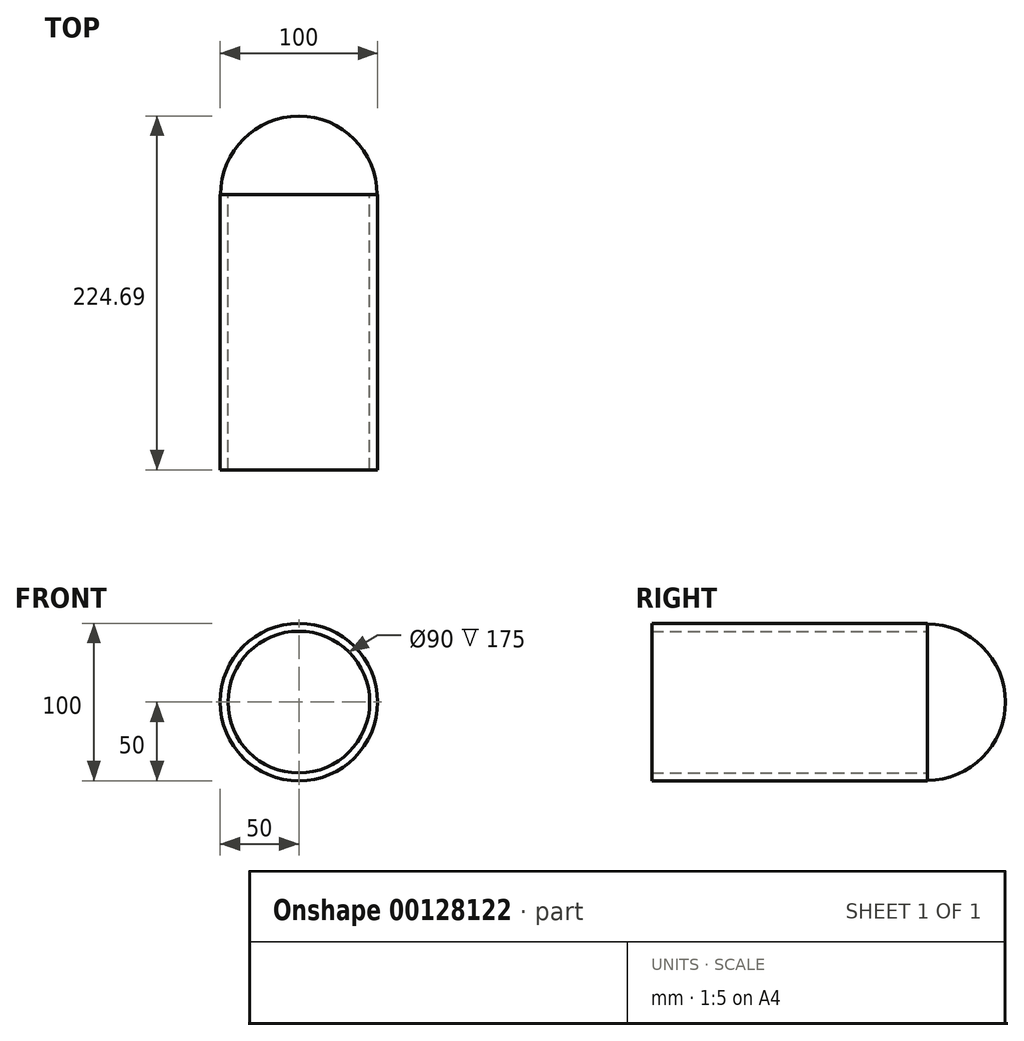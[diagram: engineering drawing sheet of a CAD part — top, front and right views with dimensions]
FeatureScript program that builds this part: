
annotation { "Feature Type Name" : "Feature", "Feature Type Description" : "" }
export const myFeature = defineFeature(function(context is Context, id is Id, definition is map)
    precondition{}
    {
        {
            var Q0;
            Q0=qCreatedBy(makeId("Front.planeOp"),FACE);
            var sketch = newSketch(context, id + "F0", { "sketchPlane" : qUnion([Q0])});
            skCircle(sketch, "E0", {"center": v(0, 0) * mm, "radius": 50 * mm});
            skSolve(sketch);
        }
        {
            var Q0;
            Q0 = qSketchRegion(id + "F0", true);
            var Q1;
            Q1=makeQuery(id+"F0.imprint","IMPRINT",FACE,{"disambiguationData":[TD([[makeQuery(id+"F0.imprint","IMPRINT",EDGE,{"derivedFrom":sQuery(id+"F0.wireOp",EDGE,"E0")}),1.0]])]});
            extrude(context, id + "F1", {"entities" : qUnion([Q0, Q1]), "depth" : 175 * mm});
        }
        {
            var Q0;
            Q0=qCreatedBy(makeId("Front.planeOp"),FACE);
            var sketch = newSketch(context, id + "F2", { "sketchPlane" : qUnion([Q0])});
            skArc(sketch, "E1", {"start": v(0, 49.7) * mm, "mid": v(-49.7, 0) * mm, "end": v(0, -49.7) * mm});
            skLineSegment(sketch, "E2", {"start": v(0, 49.7) * mm, "end": v(0, -49.7) * mm});
            skLineSegment(sketch, "E3", {"start": v(0, -49.7) * mm, "end": v(0, 74.72) * mm, "construction": true});
            skLineSegment(sketch, "E4", {"start": v(0, 74.72) * mm, "end": v(0, -74.72) * mm, "construction": true});
            skSolve(sketch);
        }
        {
            var Q0;
            Q0 = qSketchRegion(id + "F2", true);
            var Q1;
            Q1=sQuery(id+"F2.wireOp",EDGE,"E4");
            revolve(context, id + "F3", {"operationType" : NewBodyOperationType.ADD, "entities" : qUnion([Q0]), "axis" : qUnion([Q1]), "revolveType" : RevolveType.FULL});
        }
        {
            var Q0;
            Q0=qCreatedBy(makeId("Front.planeOp"),FACE);
            var sketch = newSketch(context, id + "F4", { "sketchPlane" : qUnion([Q0])});
            skCircle(sketch, "E5", {"center": v(0, 0) * mm, "radius": 46.92 * mm});
            skSolve(sketch);
        }
        {
            var Q0;
            Q0=sQuery(id+"F4.wireOp",VERTEX,"E5.center");
            var Q1;
            Q1=makeQuery(id+"F1.opExtrude","SWEPT_BODY",BODY,{"disambiguationData":[OSD([sQuery(id+"F0.wireOp",EDGE,"E0")])]});
            hole(context, id + "F5", {"style" : HoleStyle.SIMPLE, "endStyle" : HoleEndStyle.THROUGH, "oppositeDirection" : true, "holeDiameter" : 90 * mm, "locations" : qUnion([Q0]), "scope" : qUnion([Q1]), "isTappedThrough" : true});
        }
    });
